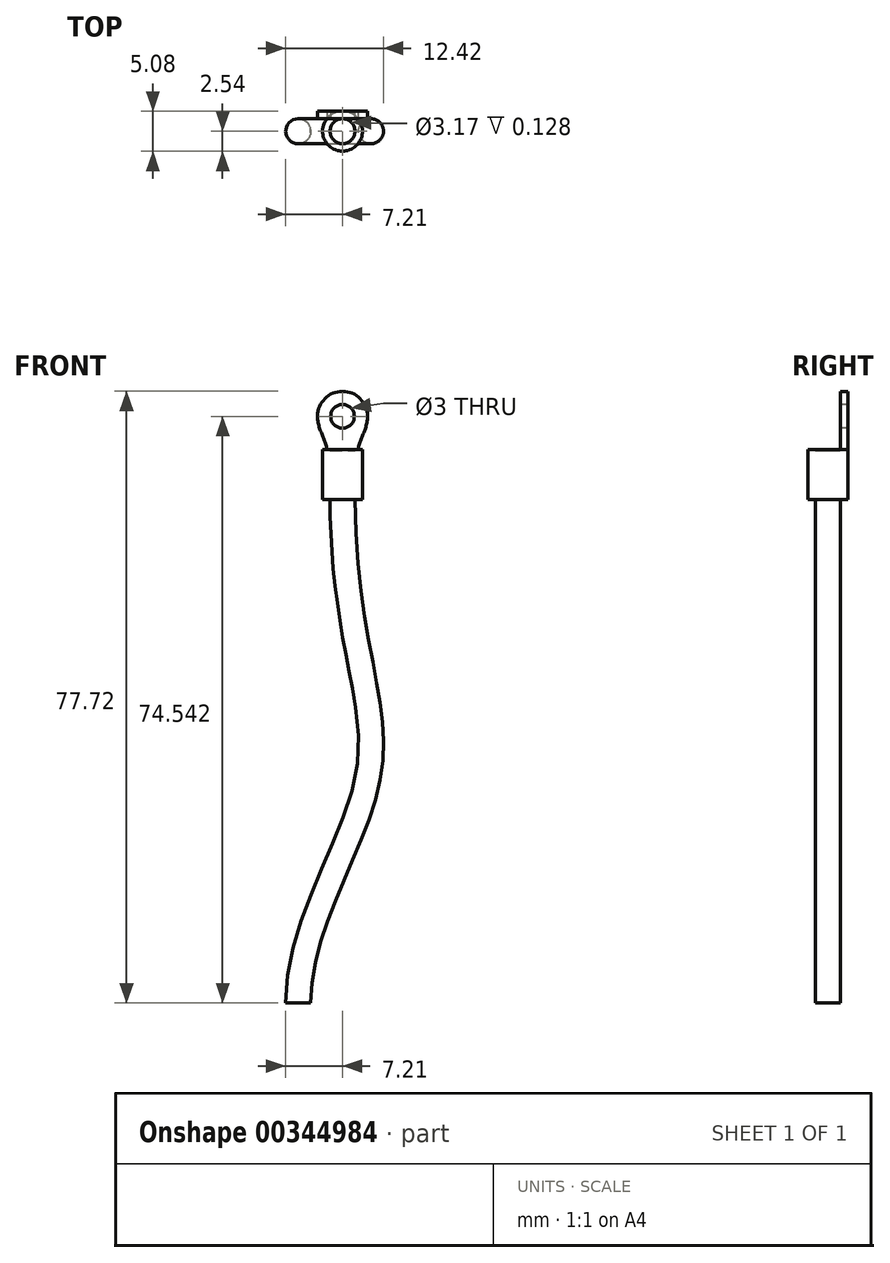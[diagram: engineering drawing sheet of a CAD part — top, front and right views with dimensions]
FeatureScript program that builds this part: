
annotation { "Feature Type Name" : "Feature", "Feature Type Description" : "" }
export const myFeature = defineFeature(function(context is Context, id is Id, definition is map)
    precondition{}
    {
        {
            var Q0;
            Q0=qCreatedBy(makeId("Top.planeOp"),FACE);
            var sketch = newSketch(context, id + "F0", { "sketchPlane" : qUnion([Q0])});
            skCircle(sketch, "E0", {"center": v(0, 0) * mm, "radius": 1.59 * mm});
            skCircle(sketch, "E1", {"center": v(0, 0) * mm, "radius": 2.54 * mm});
            skSolve(sketch);
        }
        {
            var Q0;
            Q0 = qSketchRegion(id + "F0", true);
            extrude(context, id + "F1", {"entities" : qUnion([Q0]), "depth" : 6.35 * mm});
        }
        {
            var Q0;
            Q0=makeQuery(id+"F1.opExtrude","CAP_FACE",FACE,{"disambiguationData":[OSD([sQuery(id+"F0.wireOp",EDGE,"E0"),sQuery(id+"F0.wireOp",EDGE,"E1")])],"isStart":false});
            var sketch = newSketch(context, id + "F2", { "sketchPlane" : qUnion([Q0])});
            skLineSegment(sketch, "E2.bottom", {"start": v(5.24, 2.54) * mm, "end": v(-5.56, 2.54) * mm});
            skLineSegment(sketch, "E2.top", {"start": v(5.24, 1.6) * mm, "end": v(-5.56, 1.6) * mm});
            skLineSegment(sketch, "E2.left", {"start": v(5.24, 2.54) * mm, "end": v(5.24, 1.6) * mm});
            skLineSegment(sketch, "E2.right", {"start": v(-5.56, 2.54) * mm, "end": v(-5.56, 1.6) * mm});
            skSolve(sketch);
        }
        {
            var Q0;
            Q0 = qSketchRegion(id + "F2", true);
            extrude(context, id + "F3", {"entities" : qUnion([Q0]), "operationType" : NewBodyOperationType.ADD, "depth" : 25.4 * mm});
        }
        {
            var Q0;
            Q0=makeQuery(id+"F3.opExtrude","SWEPT_FACE",FACE,{"disambiguationData":[OSD([sQuery(id+"F2.wireOp",EDGE,"E2.top")])]});
            var sketch = newSketch(context, id + "F4", { "sketchPlane" : qUnion([Q0])});
            skCircle(sketch, "E3", {"center": v(0, 10.54) * mm, "radius": 3.18 * mm});
            skCircle(sketch, "E4", {"center": v(0, 10.54) * mm, "radius": 1.5 * mm});
            skFitSpline(sketch, "E5", {"points": [v(3.17, 10.57) * mm, v(1.98, 6.35) * mm], "startDerivative": vector(0.04, -4.92) * mm, "endDerivative": vector(-0.65, -4.24) * mm});
            skFitSpline(sketch, "E6.MirrorCS", {"points": [v(-3.17, 10.57) * mm, v(-1.98, 6.35) * mm], "startDerivative": vector(-0.04, -4.92) * mm, "endDerivative": vector(0.65, -4.24) * mm});
            skLineSegment(sketch, "E7.bottom", {"start": v(5.95, 32.46) * mm, "end": v(-6.6, 32.46) * mm});
            skLineSegment(sketch, "E7.top", {"start": v(5.95, 6.35) * mm, "end": v(-6.6, 6.35) * mm});
            skLineSegment(sketch, "E7.left", {"start": v(5.95, 32.46) * mm, "end": v(5.95, 6.35) * mm});
            skLineSegment(sketch, "E7.right", {"start": v(-6.6, 32.46) * mm, "end": v(-6.6, 6.35) * mm});
            skSolve(sketch);
        }
        {
            var Q0;
            {var subQ0=sQuery(id+"F4.wireOp",EDGE,"E5");Q0=makeQuery(id+"F4.imprint","IMPRINT",FACE,{"disambiguationData":[TD([[makeQuery(id+"F4.imprint","IMPRINT",EDGE,{"derivedFrom":subQ0}),1.0]])]});}
            extrude(context, id + "F5", {"entities" : qUnion([Q0]), "operationType" : NewBodyOperationType.REMOVE, "oppositeDirection" : true, "depth" : 25.4 * mm});
        }
        {
            var Q0;
            Q0=makeQuery(id+"F4.imprint","IMPRINT",FACE,{"disambiguationData":[TD([[makeQuery(id+"F4.imprint","IMPRINT",EDGE,{"derivedFrom":sQuery(id+"F4.wireOp",EDGE,"E4")}),1.0]])]});
            extrude(context, id + "F6", {"entities" : qUnion([Q0]), "operationType" : NewBodyOperationType.REMOVE, "oppositeDirection" : true, "depth" : 25.4 * mm});
        }
        {
            var Q0;
            Q0=qCreatedBy(makeId("Front.planeOp"),FACE);
            var sketch = newSketch(context, id + "F7", { "sketchPlane" : qUnion([Q0])});
            skLineSegment(sketch, "E8", {"start": v(0, 0) * mm, "end": v(0, 6.22) * mm});
            skFitSpline(sketch, "E9", {"points": [v(0, 0) * mm, v(3.25, -35.3) * mm, v(-5.62, -63.98) * mm], "startDerivative": vector(0, -104.64) * mm, "endDerivative": vector(0.55, -63.5) * mm});
            skSolve(sketch);
        }
        {
            var Q0;
            Q0=makeQuery(id+"F0.imprint","IMPRINT",FACE,{"disambiguationData":[TD([[makeQuery(id+"F0.imprint","IMPRINT",EDGE,{"derivedFrom":sQuery(id+"F0.wireOp",EDGE,"E0")}),1.0]])]});
            var Q1;
            Q1=sQuery(id+"F7.wireOp",EDGE,"E8");
            sweep(context, id + "F8", {"operationType" : NewBodyOperationType.ADD, "profiles" : qUnion([Q0]), "path" : qUnion([Q1])});
        }
        {
            var Q0;
            Q0=makeQuery(id+"F0.imprint","IMPRINT",FACE,{"disambiguationData":[TD([[makeQuery(id+"F0.imprint","IMPRINT",EDGE,{"derivedFrom":sQuery(id+"F0.wireOp",EDGE,"E0")}),1.0]])]});
            var Q1;
            Q1=sQuery(id+"F7.wireOp",EDGE,"E9");
            sweep(context, id + "F9", {"operationType" : NewBodyOperationType.ADD, "profiles" : qUnion([Q0]), "path" : qUnion([Q1])});
        }
    });
